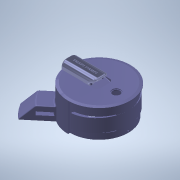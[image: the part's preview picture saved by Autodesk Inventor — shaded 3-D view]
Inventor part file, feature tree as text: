
AUTODESK INVENTOR PART (.ipt)
format: ipt  version: 2020 (Build 240168000, 168)  size: 4,229,120 bytes
history: native  units: mm
features: extrude x60, sketch x25, fillet x22, other x14, plane x11, projected_geometry x8, boolean_combine x7, thread x7, hole x4, revolve x3, shell x3, chamfer x3, move_body x1
ambient origin geometry x8: Origin, YZ Plane, XZ Plane, XY Plane, X Axis, Y Axis, Z Axis, Center Point
bodies: Solid7 (feature_tree), Solid8 (feature_tree), Solid9 (feature_tree), Solid13 (feature_tree)
feature tree (168):
  other  "AroPrincipal"
  extrude  "Extrusion1"  Depth=2.5mm
  sketch  "Sketch3"  dims[d0=90.0mm d1=2.5mm]
  extrude  "Patitas"  Depth=24.43461mm
  revolve  "Revolution1"  [1 undecoded]
  plane  "Work Plane1"
  extrude  "Extrusion3"  Depth=15.0mm
  sketch  "Sketch7"  dims[d7=180.0mm d8=15.0mm]
  revolve  "Revolution2"  [1 undecoded]
  revolve  "Revolution3"  [1 undecoded]
  extrude  "Extrusion4"  Depth=20.0mm
  plane  "Work Plane2"
  extrude  "Extrusion5"  Depth=15.0mm
  extrude  "Extrusion6"  Depth=5.0mm
  plane  "Work Plane3"
  extrude  "Extrusion7"  Depth=7.5mm
  sketch  "Sketch11"  dims[d20=15.0mm d21=15.0mm]
  extrude  "Extrusion10"  TaperAngle=90.0deg  [1 undecoded]
  extrude  "Extrusion11"  Depth=90.0mm
  extrude  "Extrusion17"  Depth=85.0mm
  plane  "Work Plane4"
  move_body  "Move Body2"
  extrude  "Extrusion21"  Depth=16.580628mm
  plane  "Work Plane5"
  extrude  "Extrusion22"  Depth=10.0mm
  plane  "Work Plane6"
  extrude  "Extrusion23"  Depth=20.0mm
  sketch  "Sketch24"  dims[d24=20.0mm d25=7.5mm]
  extrude  "Extrusion24"  Depth=1.0mm
  extrude  "Extrusion25"  Depth=85.0mm
  shell  "Shell1"  Thickness=43.0mm
  shell  "Shell2"  Thickness=96.0mm
  hole  "Hole1"  [1 undecoded]
  hole  "Hole2"  [1 undecoded]
  boolean_combine  "Combine3"
  extrude  "Extrusion26"  Depth=10.0mm TaperAngle=0.0deg
  extrude  "Extrusion27"  Depth=3.0mm
  sketch  "Sketch25"  dims[d26=5.0mm d27=90.0deg]
  extrude  "Extrusion28"  Depth=43.0mm
  plane  "Work Plane7"
  sketch  "Sketch26"  dims[d28=10.0mm d29=90.0mm]
  extrude  "Extrusion30"  Depth=2.5mm TaperAngle=0.0deg
  extrude  "Extrusion31"  Depth=14.2mm
  thread  "Thread2"  [1 undecoded]
  thread  "Thread3"  [1 undecoded]
  thread  "Thread4"  [1 undecoded]
  extrude  "Extrusion32"  Depth=2.0mm
  boolean_combine  "Combine4"
  fillet  "Fillet4"  Radius=4.6mm
  fillet  "Fillet8"  Radius=2.2mm
  fillet  "Fillet9"  Radius=6.0mm
  plane  "Work Plane8"
  sketch  "Sketch30"  dims[d37=20.0mm d38=0.0mm d39=16.580628mm]
  extrude  "Extrusion33"  Depth=6.8mm
  extrude  "Extrusion34"  Depth=20.0mm
  fillet  "fillet hold screw core"  Radius=40.0mm
  extrude  "Extrusion36"  Depth=25.0mm
  fillet  "Fillet11"  Radius=1.1mm
  hole  "Hole3"  [1 undecoded]
  extrude  "Extrusion37"  Depth=8.0mm
  fillet  "Fillet12"  Radius=15.0mm
  plane  "Work Plane9"
  extrude  "Extrusion38"  Depth=5.0mm TaperAngle=0.0deg
  extrude  "Extrusion39"  Depth=31.4mm
  fillet  "Fillet13"  Radius=31.4mm
  fillet  "Fillet14"  Radius=3.5mm
  extrude  "Extrusion40"  Depth=0.5mm
  extrude  "Extrusion41"  Depth=14.2mm
  other  "Battery holder 1"
  extrude  "Battery holder"  Depth=31.4mm
  hole  "Hole4"  [1 undecoded]
  extrude  "Extrusion44"  Depth=6.0mm TaperAngle=0.0deg
  extrude  "Extrusion45"  Depth=96.0mm
  extrude  "Extrusion46"  [1 undecoded]
  extrude  "Extrusion47"  TaperAngle=0.0deg  [1 undecoded]
  extrude  "Extrusion48"  Depth=2.5mm TaperAngle=0.0deg
  extrude  "Extrusion49"  Depth=8.5mm
  extrude  "Extrusion50"  Depth=96.0mm
  extrude  "Extrusion51"  Depth=85.0mm
  extrude  "Extrusion52"  Depth=96.0mm
  fillet  "Fillet15"  Radius=35.0mm
  chamfer  "Chamfer1"  Distance=1.5mm
  sketch  "Sketch36"  dims[d51=10.0mm d52=2.0mm d53=35.0mm d54=4.0mm d55=2.0mm]
  extrude  "Extrusion53"  Depth=2.0mm
  extrude  "Extrusion56"  Depth=2.0mm
  extrude  "Extrusion57"  Depth=3.0mm
  extrude  "Extrusion58"  Depth=30.0mm
  thread  "Thread5"  [1 undecoded]
  thread  "Thread6"  [1 undecoded]
  thread  "Thread7"  [1 undecoded]
  thread  "Thread8"  [1 undecoded]
  chamfer  "Chamfer2"  Distance=35.0mm
  fillet  "Fillet17"  Radius=15.0mm
  other  "tapa PPG"
  other  "tapa up PPG"
  extrude  "Extrusion61"  Depth=30.0mm
  sketch  "Sketch41"  dims[d56=3.0mm d57=96.0mm]
  extrude  "Extrusion66"  Depth=1.5mm
  fillet  "Fillet19"  Radius=14.0mm
  boolean_combine  "Combine5"
  boolean_combine  "Combine6"
  shell  "Shell4"  Thickness=7.0mm
  extrude  "Extrusion67"  Depth=7.0mm
  other  "plano sup sup"
  extrude  "Extrusion68"  Depth=7.0mm
  extrude  "Extrusion69"  Depth=7.0mm
  fillet  "Fillet22"  Radius=12.0mm
  fillet  "Fillet23"  Radius=12.0mm
  fillet  "Fillet24"  Radius=10.0mm
  boolean_combine  "Combine7"
  fillet  "Fillet25"  Radius=12.0mm
  extrude  "Extrusion70"  Depth=2.0mm
  boolean_combine  "Combine8"
  extrude  "Extrusion71"  Depth=1.5mm
  fillet  "Fillet26"  Radius=1.5mm
  fillet  "Fillet28"  Radius=4.0mm
  fillet  "Fillet29"  Radius=2.0mm
  chamfer  "Chamfer3"  Distance=4.0mm
  boolean_combine  "Combine10"
  fillet  "Fillet30"  Radius=2.0mm
  extrude  "Extrusion72"  Depth=14.0mm TaperAngle=0.0deg
  fillet  "Fillet31"  Radius=10.0mm
  fillet  "Fillet32"  Radius=34.0mm
  fillet  "Fillet33"  Radius=10.5mm
  extrude  "Extrusion73"  Depth=0.5mm
  extrude  "Extrusion74"  Depth=10.0mm
  extrude  "Extrusion75"  Depth=2.5mm
  extrude  "Extrusion76"  Depth=36.1mm TaperAngle=0.0deg
  plane  "Work Plane11"
  extrude  "Extrusion77"  [1 undecoded]
  plane  "Work Plane12"
  sketch  "Sketch46"  dims[d66=96.0mm d67=2.5mm d68=0.0mm]
  extrude  "Extrusion78"  Depth=2.5mm
  extrude  "Extrusion79"  Depth=1.5mm
  sketch  "Sketch47"  dims[d78=18.54mm d79=14.2mm d80=15.0mm d81=11.43mm d82=2.0mm d83=2.0mm d84=4.6mm d85=2.2mm d86=6.0mm d87=6.8mm d88=20.0mm d90=40.0mm d91=25.0mm d94=1.1mm d95=12.5mm d96=8.0mm d97=15.0mm d98=0.0mm d110=5.0mm d111=0.0mm d122=31.4mm d123=31.4mm d124=3.5mm d125=0.5mm d126=14.2mm d131=31.4mm d132=16.1mm d139=6.0mm d140=0.0mm d144=96.0mm d145=-48.0mm d152=0.0mm d153=-17.5mm d154=0.0mm d163=2.5mm d164=0.0mm d171=8.5mm d172=96.0mm d173=85.0mm d174=96.0mm d175=35.0mm d176=1.5mm d177=2.0mm d178=2.0mm d179=3.0mm d180=30.0mm d181=2.0mm d182=0.0mm d183=3.0mm d184=85.0mm d185=85.0mm d186=35.0mm d188=15.0mm d189=30.0mm d190=1.5mm d191=14.0mm d192=0.0mm d195=7.0mm d196=7.0mm d197=7.0mm d198=7.0mm d199=12.0mm d200=12.0mm d201=10.0mm d202=0.0mm d203=12.0mm d204=0.0mm d205=2.0mm d206=1.5mm d207=1.5mm d208=7.0mm d209=6.0mm d210=4.0mm d211=2.0mm d212=90.0deg d213=8.0mm d214=20.594885mm d215=7.0mm d216=6.0mm d217=4.0mm d218=2.0mm d219=90.0deg d220=8.0mm d221=20.594885mm d222=4.0mm d223=2.0mm d224=4.0mm d225=2.0mm d226=14.0mm d227=0.0mm d228=10.0mm d229=34.0mm d230=10.5mm d231=0.0mm d232=0.5mm d233=10.0mm d234=2.5mm d235=36.1mm d236=0.0mm d239=-42.5mm d242=2.5mm d243=1.5mm d244=3.0mm d245=2.5mm d246=1.5mm d247=3.0mm d249=0.15mm d251=54.0mm d252=0.0mm d254=10.0mm d255=34.0mm d256=3.0mm d257=3.0mm d258=3.0mm d259=5.0mm d260=5.0mm d261=5.0mm d262=5.0mm d263=5.0mm d264=3.5mm d265=0.0mm d268=3.5mm d269=0.0mm d270=3.5mm d271=0.0mm d272=3.5mm d273=0.0mm d274=3.5mm d275=0.0mm d276=10.0mm d280=5.0mm d282=10.5mm d283=1.0mm d284=0.5mm d285=1.0mm d286=0.75mm d287=6.5mm d288=96.0mm d289=85.0mm d290=96.0mm d291=35.0mm d292=1.5mm d293=2.0mm d294=2.0mm d295=3.0mm d296=30.0mm d297=2.0mm d298=0.0mm d299=25.0mm d300=3.0mm d301=0.0mm d302=10.0mm d303=2.25mm d304=10.0mm d307=2.0mm d308=0.0mm d309=1.5mm d310=3.0mm d311=4.5mm d312=5.0mm d313=3.0mm d314=2.5mm d315=3.0mm d316=5.98424mm d317=3.023mm d318=2.0mm d319=14.3117mm d320=2.0mm d321=0.0mm d322=1.5mm d323=1.5mm d324=58.5mm d325=0.0mm d326=1.0mm d327=0.25mm d328=23.9mm d329=85.0mm d332=1.3mm d333=0.0mm d334=10.0mm d335=5.0mm d336=45.0deg d337=0.4mm d338=0.0mm d339=0.25mm d340=0.2mm d346=0.1mm d347=0.1mm d348=0.1mm d349=1.0mm d350=0.75mm d352=0.5mm d353=1.3mm d354=0.0mm d355=0.5mm d356=0.0mm d357=0.5mm d358=85.0mm d359=90.0deg d360=25.0mm d361=96.0mm d362=38.0mm d367=20.0mm d368=0.0mm d369=1.5mm d370=14.67mm d371=0.0mm d372=20.0mm d373=6.0mm d374=4.0mm d375=2.0mm d376=90.0deg d377=12.67mm d378=0.0mm d381=6.17mm d382=0.0mm d383=4.67mm d384=0.0mm d385=4.67mm d386=0.0mm d387=6.5mm d388=13.438mm d389=3.2mm d390=0.5mm d391=0.7mm d392=13.17mm d393=0.0mm d394=13.17mm d395=0.0mm d396=0.5mm d397=3.25mm d406=0.0mm d409=13.0mm d411=10.0mm d412=0.0mm d413=6.5mm d414=1.5mm d415=1.5mm d416=3.5mm d417=6.5mm d418=1.5mm d419=0.5mm d420=0.7mm d421=2.5mm d422=0.0mm d423=2.5mm d424=0.0mm d425=2.5mm d426=0.0mm d427=2.0mm d428=0.5mm d429=5.0mm d430=7.25mm d431=45.0deg d432=8.0mm d433=20.0mm d434=1.25mm d435=85.0mm d436=20.0mm d437=1.25mm d438=2.0mm d439=0.0mm d440=90.0mm d441=180.0mm d442=85.0mm d443=73.0mm d452=6.0mm d458=2.0mm d459=2.0mm d460=96.0mm d461=2.0mm d462=2.0mm d463=4.0mm d464=8.0mm d465=8.0mm d466=4.0mm d467=4.0mm d468=4.0mm d469=4.0mm d470=6.0mm d471=6.0mm d472=3.0mm d473=3.0mm d474=3.0mm d475=3.0mm d476=5.0mm d477=0.0mm d478=2.0mm d479=0.0mm d480=5.0mm d481=0.0mm d482=3.5mm d483=0.0mm d484=3.5mm d485=0.0mm d486=3.5mm d487=0.0mm d488=3.5mm d489=0.0mm d490=5.0mm d491=2.0mm d492=45.0deg d493=5.0mm d504=15.0mm d512=60.0deg d534=4.0mm d535=2.0mm d536=10.0mm d545=10.0mm d548=15.0mm d549=4.363323mm d550=4.0mm d551=2.0mm d552=10.0mm d553=10.0mm d554=15.0mm d555=2.5mm d558=25.0mm d559=0.0mm d576=96.0mm d577=70.0mm d578=20.0mm d579=7.0mm d580=10.5mm d581=0.0mm d582=8.5mm d583=2.0mm d584=25.0mm d585=0.0mm d586=55.5mm d587=96.0mm d588=70.0mm d589=25.0mm d590=10.0mm d591=0.0mm d592=2.0mm d593=0.0mm d596=177.0mm d597=17.75mm d598=11.0mm d599=17.75mm d600=11.0mm d601=10.0mm d602=10.0mm d603=6.0mm d604=10.0mm d605=0.0mm d606=40.0mm d607=12.5mm d608=0.0mm d609=0.0mm d610=8.0mm d611=2.0mm d612=10.0mm d616=1.0mm d617=2.0mm d618=5.0mm d619=0.5mm d620=4.0mm d621=1.0mm d622=45.0deg d623=1.0mm d624=9.0mm d625=2.75mm d626=40.0mm d627=1.5mm d628=0.0mm d629=0.5mm d630=27.0mm d631=4.0mm d632=1.0mm d633=2.0mm d634=1.0mm d635=1.0mm d636=20.0mm d637=0.0mm d638=15.0mm d639=0.0mm d640=2.5mm d641=0.0mm d642=2.5mm d643=0.0mm d644=-0.5mm d645=0.5mm d646=0.0mm d647=45.5mm d648=35.011113mm d649=13.22mm d650=17.5mm d651=11.2mm d652=1.12mm d653=0.0mm d654=2.5mm d655=0.0mm d656=10.0mm d657=35.0mm d659=2.0mm d660=2.0mm d661=8.0mm d662=17.5mm d663=4.75mm d664=1.0mm d665=45.0mm d666=0.0mm d667=44.749mm d668=0.0mm]
  extrude  "Extrusion80"  Depth=3.0mm
  extrude  "Extrusion81"  Depth=2.5mm
  sketch  "Sketch5"  dims[d2=43.0mm d3=0.0mm d4=24.43461mm]
  sketch  "Sketch6"  dims[d5=90.0mm d6=6.981317mm]
  other  "Enganche"
  sketch  "Sketch8"  dims[d9=15.0mm d11=20.0mm d12=0.0mm]
  sketch  "Sketch9"  dims[d15=20.0mm d16=90.0mm]
  projected_geometry  "Projected Loop1"
  sketch  "Sketch10"  dims[d18=180.0deg d19=20.0mm]
  other  "tapa"
  projected_geometry  "Projected Loop2"
  other  "Fingertip"
  sketch  "Sketch20"  dims[d22=25.0mm d23=5.0mm]
  other  "inf RR"
  other  "reflector"
  projected_geometry  "Projected Loop7"
  projected_geometry  "Projected Loop8"
  projected_geometry  "Projected Loop9"
  sketch  "Sketch28"  dims[d30=96.0mm d36=85.0mm]
  sketch  "Sketch31"  dims[d40=16.580628mm d41=10.0mm]
  other  "tapa RR"
  sketch  "Sketch32"  dims[d42=2.5mm d43=20.0mm]
  sketch  "Sketch33"  dims[d44=29.84513mm d45=1.0mm]
  sketch  "Sketch34"  dims[d46=0.174533mm d47=85.0mm d48=43.0mm d49=0.0mm d50=96.0mm]
  other  "forma dedo"
  other  "PPG cover"
  sketch  "Sketch42"  dims[d58=2.0mm d59=10.0mm d60=0.0mm]
  other  "forma dedo sup"
  sketch  "Sketch44"  dims[d61=35.0mm d62=3.0mm]
  sketch  "Sketch45"  dims[d63=30.0mm d64=0.0mm d65=43.0mm]
  projected_geometry  "Project Cut Edges1"
  projected_geometry  "Project Cut Edges2"
  projected_geometry  "Project Cut Edges3"
note: 18 required parameter values undecoded (feature->parameter linkage not recoverable at this tier; creation-order binding heuristic only, values carry confidence <= 0.55)